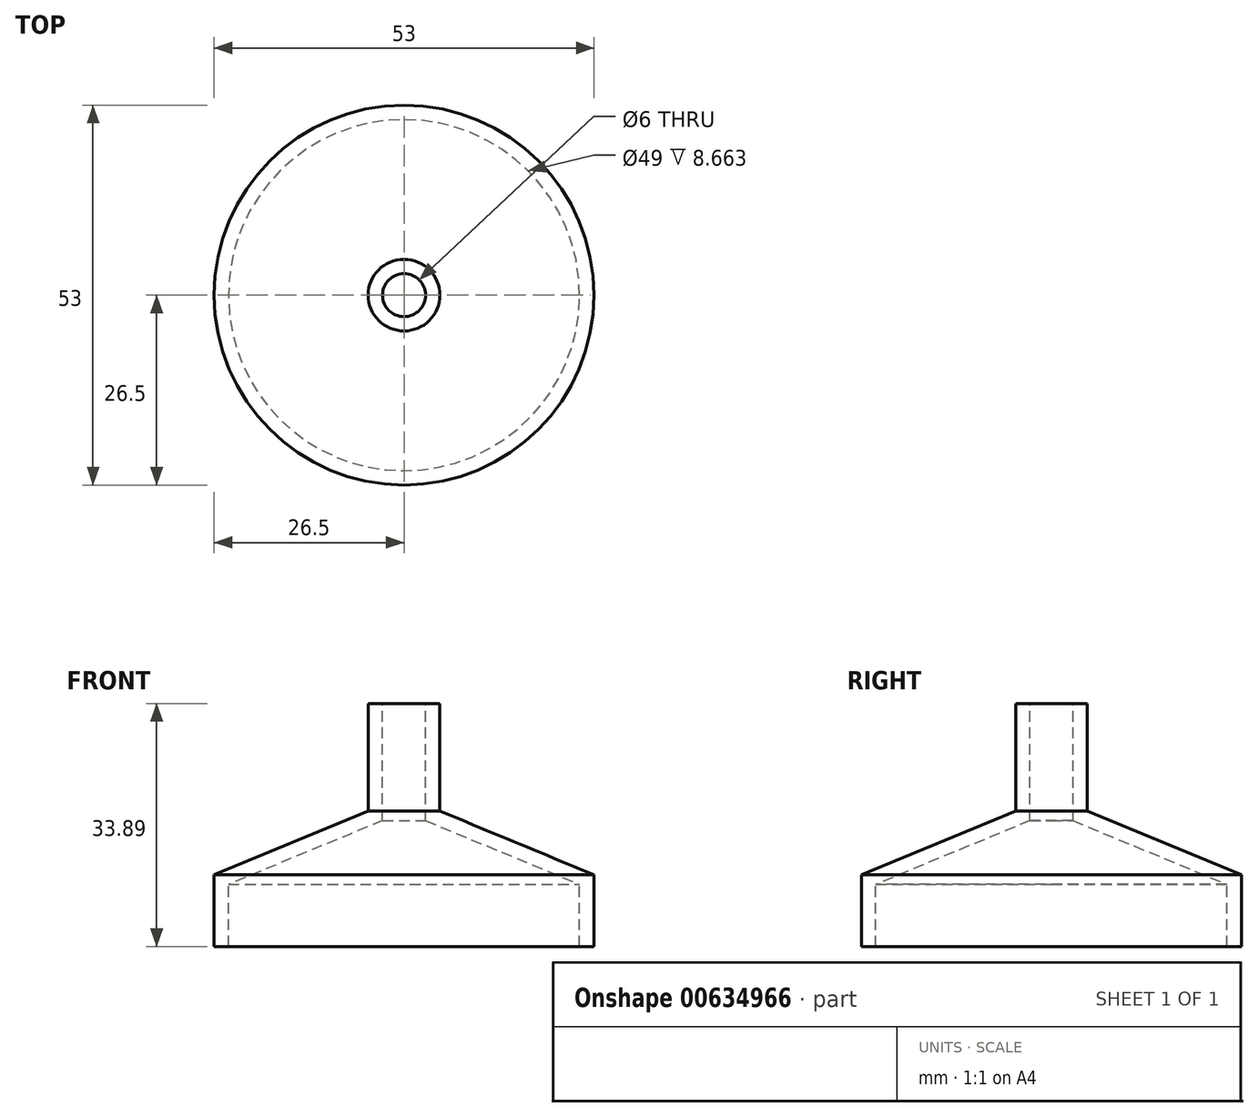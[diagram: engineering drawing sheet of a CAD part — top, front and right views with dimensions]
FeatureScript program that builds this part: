
annotation { "Feature Type Name" : "Feature", "Feature Type Description" : "" }
export const myFeature = defineFeature(function(context is Context, id is Id, definition is map)
    precondition{}
    {
        {
            var Q0;
            Q0=qCreatedBy(makeId("Right.planeOp"),FACE);
            var sketch = newSketch(context, id + "F0", { "sketchPlane" : qUnion([Q0])});
            skLineSegment(sketch, "E0", {"start": v(-5, 15.97) * mm, "end": v(-5, 0.97) * mm});
            skLineSegment(sketch, "E1", {"start": v(-5, 0.97) * mm, "end": v(-26.5, -7.92) * mm});
            skLineSegment(sketch, "E2", {"start": v(-26.5, -7.92) * mm, "end": v(-26.5, -17.92) * mm});
            skLineSegment(sketch, "E3", {"start": v(0, 24.02) * mm, "end": v(0, -24.83) * mm, "construction": true});
            skLineSegment(sketch, "E4", {"start": v(-33.48, -17.92) * mm, "end": v(28.77, -17.92) * mm, "construction": true});
            skLineSegment(sketch, "E5", {"start": v(-5, 15.97) * mm, "end": v(0, 15.97) * mm});
            skLineSegment(sketch, "E6", {"start": v(0, 15.97) * mm, "end": v(0, -17.92) * mm});
            skLineSegment(sketch, "E7", {"start": v(-26.5, -17.92) * mm, "end": v(0, -17.92) * mm});
            skSolve(sketch);
        }
        {
            var Q0;
            Q0 = qSketchRegion(id + "F0", true);
            var Q1;
            Q1=sQuery(id+"F0.wireOp",EDGE,"E3");
            revolve(context, id + "F1", {"entities" : qUnion([Q0]), "axis" : qUnion([Q1]), "revolveType" : RevolveType.FULL, "surfaceOperationType" : NewSurfaceOperationType.NEW});
        }
        {
            var Q0;
            Q0=makeQuery(id+"F1.opRevolve","SWEPT_FACE",FACE,{"disambiguationData":[OSD([sQuery(id+"F0.wireOp",EDGE,"E7")])]});
            var Q1;
            Q1=makeQuery(id+"F1.opRevolve","SWEPT_FACE",FACE,{"disambiguationData":[OSD([sQuery(id+"F0.wireOp",EDGE,"E5")])]});
            shell(context, id + "F2", {"entities" : qUnion([Q0, Q1]), "thickness" : 2 * mm});
        }
        {
            var Q0;
            Q0=makeQuery(id+"F1.opRevolve","SWEPT_FACE",FACE,{"disambiguationData":[OSD([sQuery(id+"F0.wireOp",EDGE,"E7")])]});
            var sketch = newSketch(context, id + "F3", { "sketchPlane" : qUnion([Q0])});
            skCircle(sketch, "E8", {"center": v(0, 0) * mm, "radius": 26.51 * mm, "construction": true});
            skLineSegment(sketch, "E9", {"start": v(0, 32.43) * mm, "end": v(0, -32.47) * mm, "construction": true});
            skLineSegment(sketch, "E10", {"start": v(-43.3, 0) * mm, "end": v(38.86, 0) * mm, "construction": true});
            skArc(sketch, "E11", {"start": v(26.44, -2) * mm, "mid": v(28.5, 0) * mm, "end": v(26.44, 2) * mm});
            skArc(sketch, "E12", {"start": v(-26.44, 2) * mm, "mid": v(-28.5, 0) * mm, "end": v(-26.44, -2) * mm});
            skArc(sketch, "E13", {"start": v(2, 26.44) * mm, "mid": v(0, 28.5) * mm, "end": v(-2, 26.44) * mm});
            skArc(sketch, "E14", {"start": v(-2, -26.44) * mm, "mid": v(0, -28.5) * mm, "end": v(2, -26.44) * mm});
            skArc(sketch, "E15", {"start": v(7.9, 25.31) * mm, "mid": v(6.41, 27.77) * mm, "end": v(4, 26.21) * mm});
            skArc(sketch, "E16", {"start": v(13.39, 22.89) * mm, "mid": v(12.5, 25.62) * mm, "end": v(9.8, 24.64) * mm});
            skArc(sketch, "E17", {"start": v(18.2, 19.29) * mm, "mid": v(17.94, 22.15) * mm, "end": v(15.09, 21.8) * mm});
            skArc(sketch, "E18", {"start": v(22.06, 14.7) * mm, "mid": v(22.47, 17.56) * mm, "end": v(19.6, 17.85) * mm});
            skArc(sketch, "E19", {"start": v(24.8, 9.36) * mm, "mid": v(25.83, 12.05) * mm, "end": v(23.12, 12.99) * mm});
            skArc(sketch, "E20", {"start": v(26.28, 3.54) * mm, "mid": v(27.88, 5.93) * mm, "end": v(25.44, 7.45) * mm});
            skArc(sketch, "E21", {"start": v(25.46, -7.41) * mm, "mid": v(27.89, -5.88) * mm, "end": v(26.28, -3.5) * mm});
            skArc(sketch, "E22", {"start": v(23.14, -12.95) * mm, "mid": v(25.85, -12) * mm, "end": v(24.82, -9.32) * mm});
            skArc(sketch, "E23", {"start": v(19.63, -17.82) * mm, "mid": v(22.48, -17.51) * mm, "end": v(22.09, -14.67) * mm});
            skArc(sketch, "E24", {"start": v(15.12, -21.78) * mm, "mid": v(17.97, -22.12) * mm, "end": v(18.22, -19.26) * mm});
            skArc(sketch, "E25", {"start": v(9.83, -24.62) * mm, "mid": v(12.53, -25.6) * mm, "end": v(13.42, -22.87) * mm});
            skArc(sketch, "E26", {"start": v(4.04, -26.2) * mm, "mid": v(6.45, -27.76) * mm, "end": v(7.93, -25.3) * mm});
            skArc(sketch, "E27", {"start": v(-7.89, -25.31) * mm, "mid": v(-6.4, -27.77) * mm, "end": v(-3.99, -26.21) * mm});
            skArc(sketch, "E28", {"start": v(-13.38, -22.9) * mm, "mid": v(-12.48, -25.62) * mm, "end": v(-9.78, -24.64) * mm});
            skArc(sketch, "E29", {"start": v(-18.19, -19.3) * mm, "mid": v(-17.93, -22.16) * mm, "end": v(-15.08, -21.81) * mm});
            skArc(sketch, "E30", {"start": v(-22.06, -14.7) * mm, "mid": v(-22.45, -17.55) * mm, "end": v(-19.6, -17.86) * mm});
            skArc(sketch, "E31", {"start": v(-24.8, -9.37) * mm, "mid": v(-25.83, -12.05) * mm, "end": v(-23.11, -13) * mm});
            skArc(sketch, "E32", {"start": v(-26.28, -3.55) * mm, "mid": v(-27.88, -5.93) * mm, "end": v(-25.44, -7.46) * mm});
            skArc(sketch, "E33", {"start": v(-25.44, 7.46) * mm, "mid": v(-27.88, 5.93) * mm, "end": v(-26.28, 3.55) * mm});
            skArc(sketch, "E34", {"start": v(-23.11, 13) * mm, "mid": v(-25.83, 12.05) * mm, "end": v(-24.8, 9.37) * mm});
            skArc(sketch, "E35", {"start": v(-19.6, 17.86) * mm, "mid": v(-22.45, 17.55) * mm, "end": v(-22.06, 14.7) * mm});
            skArc(sketch, "E36", {"start": v(-15.08, 21.81) * mm, "mid": v(-17.93, 22.16) * mm, "end": v(-18.19, 19.3) * mm});
            skArc(sketch, "E37", {"start": v(-9.78, 24.64) * mm, "mid": v(-12.48, 25.62) * mm, "end": v(-13.38, 22.9) * mm});
            skArc(sketch, "E38", {"start": v(-3.99, 26.21) * mm, "mid": v(-6.4, 27.77) * mm, "end": v(-7.89, 25.31) * mm});
            skSolve(sketch);
        }
        {
            var Q0;
            Q0=sQuery(id+"F3.wireOp",EDGE,"E21");
            var Q1;
            Q1=sQuery(id+"F3.wireOp",EDGE,"E11");
            var Q2;
            Q2=sQuery(id+"F3.wireOp",EDGE,"E20");
            var Q3;
            Q3=sQuery(id+"F3.wireOp",EDGE,"E19");
            var Q4;
            Q4=sQuery(id+"F3.wireOp",EDGE,"E18");
            var Q5;
            Q5=sQuery(id+"F3.wireOp",EDGE,"E17");
            var Q6;
            Q6=sQuery(id+"F3.wireOp",EDGE,"E16");
            var Q7;
            Q7=sQuery(id+"F3.wireOp",EDGE,"E15");
            var Q8;
            Q8=sQuery(id+"F3.wireOp",EDGE,"E13");
            var Q9;
            Q9=sQuery(id+"F3.wireOp",EDGE,"E38");
            var Q10;
            Q10=sQuery(id+"F3.wireOp",EDGE,"E37");
            var Q11;
            Q11=sQuery(id+"F3.wireOp",EDGE,"E36");
            var Q12;
            Q12=sQuery(id+"F3.wireOp",EDGE,"E35");
            var Q13;
            Q13=sQuery(id+"F3.wireOp",EDGE,"E34");
            var Q14;
            Q14=sQuery(id+"F3.wireOp",EDGE,"E33");
            var Q15;
            Q15=sQuery(id+"F3.wireOp",EDGE,"E12");
            var Q16;
            Q16=sQuery(id+"F3.wireOp",EDGE,"E32");
            var Q17;
            Q17=sQuery(id+"F3.wireOp",EDGE,"E31");
            var Q18;
            Q18=sQuery(id+"F3.wireOp",EDGE,"E30");
            var Q19;
            Q19=sQuery(id+"F3.wireOp",EDGE,"E29");
            var Q20;
            Q20=sQuery(id+"F3.wireOp",EDGE,"E22");
            var Q21;
            Q21=sQuery(id+"F3.wireOp",EDGE,"E23");
            var Q22;
            Q22=sQuery(id+"F3.wireOp",EDGE,"E24");
            var Q23;
            Q23=sQuery(id+"F3.wireOp",EDGE,"E25");
            var Q24;
            Q24=sQuery(id+"F3.wireOp",EDGE,"E26");
            var Q25;
            Q25=sQuery(id+"F3.wireOp",EDGE,"E14");
            var Q26;
            Q26=sQuery(id+"F3.wireOp",EDGE,"E27");
            var Q27;
            Q27=sQuery(id+"F3.wireOp",EDGE,"E28");
            extrude(context, id + "F4", {"bodyType" : ToolBodyType.SURFACE, "surfaceEntities" : qUnion([Q0, Q1, Q2, Q3, Q4, Q5, Q6, Q7, Q8, Q9, Q10, Q11, Q12, Q13, Q14, Q15, Q16, Q17, Q18, Q19, Q20, Q21, Q22, Q23, Q24, Q25, Q26, Q27]), "oppositeDirection" : true, "depth" : 10 * mm, "offsetDistance" : 25.4 * mm});
        }
    });
